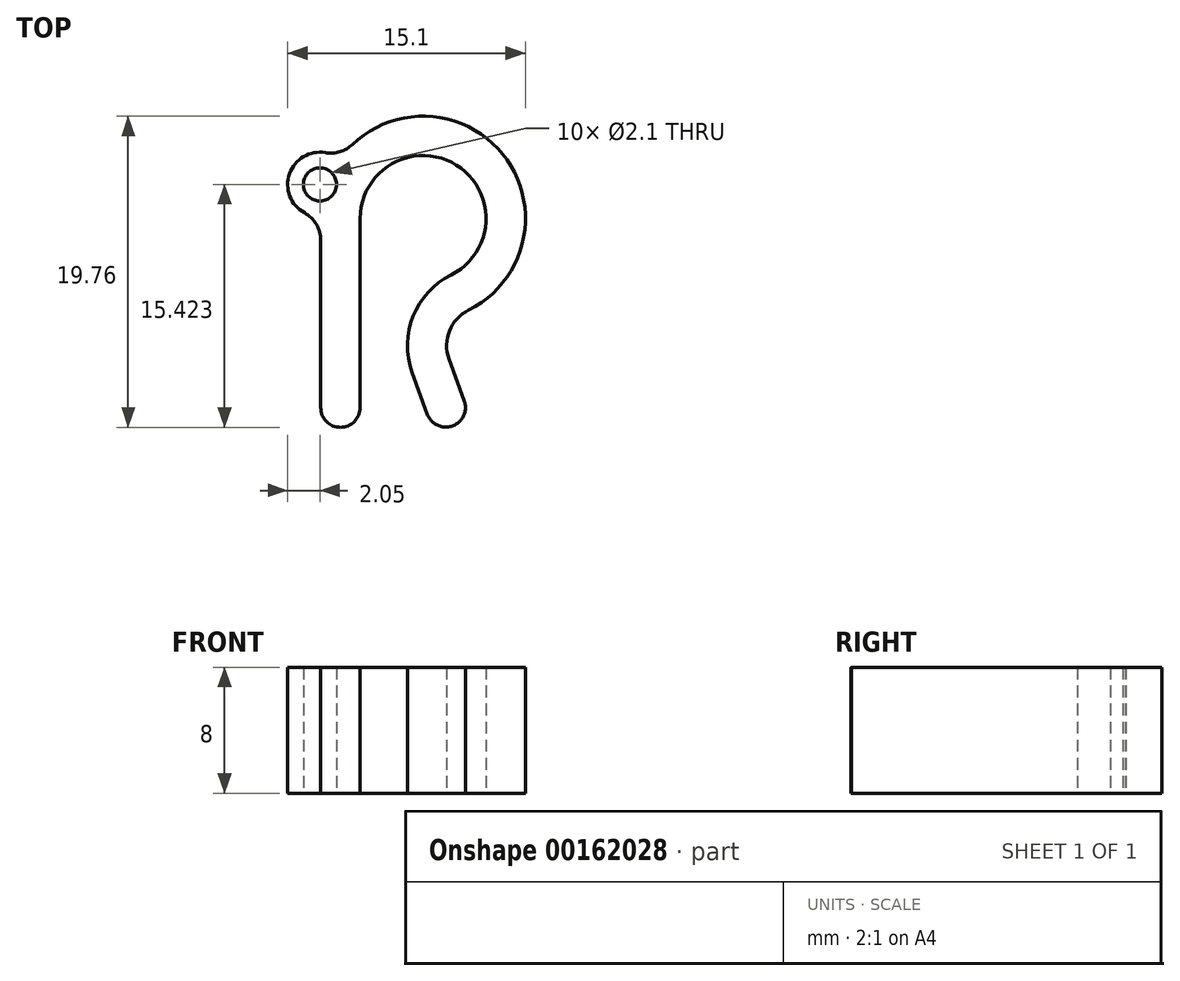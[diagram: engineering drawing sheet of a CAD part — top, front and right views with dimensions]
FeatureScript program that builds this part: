
annotation { "Feature Type Name" : "Feature", "Feature Type Description" : "" }
export const myFeature = defineFeature(function(context is Context, id is Id, definition is map)
    precondition{}
    {
        {
            var Q0;
            Q0=qCreatedBy(makeId("Top.planeOp"),FACE);
            var sketch = newSketch(context, id + "F0", { "sketchPlane" : qUnion([Q0])});
            skArc(sketch, "E0", {"start": v(1.78, -3.58) * mm, "mid": v(2.1, 3.4) * mm, "end": v(-4, 0) * mm});
            skArc(sketch, "E1", {"start": v(1.78, -3.58) * mm, "mid": v(-0.64, -6.2) * mm, "end": v(-0.7, -9.77) * mm});
            skLineSegment(sketch, "E2", {"start": v(-4, 0) * mm, "end": v(-4, -12.01) * mm});
            skLineSegment(sketch, "E3", {"start": v(-0.7, -9.77) * mm, "end": v(0.27, -12.42) * mm});
            skLineSegment(sketch, "E4.0", {"start": v(-6.5, -1.39) * mm, "end": v(-6.5, -12.01) * mm});
            skArc(sketch, "E4.1", {"start": v(2.89, -5.82) * mm, "mid": v(5.32, 3.73) * mm, "end": v(-4.48, 4.7) * mm});
            skLineSegment(sketch, "E4.2", {"start": v(1.65, -8.92) * mm, "end": v(2.62, -11.57) * mm});
            skArc(sketch, "E5.0", {"start": v(2.89, -5.82) * mm, "mid": v(1.68, -7.13) * mm, "end": v(1.65, -8.92) * mm});
            skArc(sketch, "E6", {"start": v(-6.5, -12.01) * mm, "mid": v(-5.25, -13.26) * mm, "end": v(-4, -12.01) * mm});
            skArc(sketch, "E7", {"start": v(0.27, -12.42) * mm, "mid": v(1.87, -13.17) * mm, "end": v(2.62, -11.57) * mm});
            skLineSegment(sketch, "E8", {"start": v(-5.25, -12.01) * mm, "end": v(1.44, -12) * mm, "construction": true});
            skCircle(sketch, "E9", {"center": v(-6.55, 2.16) * mm, "radius": 1.05 * mm});
            skArc(sketch, "E10.0", {"start": v(-6.2, 4.18) * mm, "mid": v(-8.49, 2.84) * mm, "end": v(-7.54, 0.37) * mm});
            skArc(sketch, "E11.filletArc", {"start": v(-6.5, -1.39) * mm, "mid": v(-6.78, -0.37) * mm, "end": v(-7.54, 0.37) * mm});
            skArc(sketch, "E12.filletArc", {"start": v(-6.2, 4.18) * mm, "mid": v(-5.28, 4.24) * mm, "end": v(-4.48, 4.7) * mm});
            skSolve(sketch);
        }
        {
            var Q0;
            Q0=qSketchRegion(id+"F0",true);
            extrude(context, id + "F1", {"entities" : qUnion([Q0]), "depth" : 8 * mm});
        }
    });
